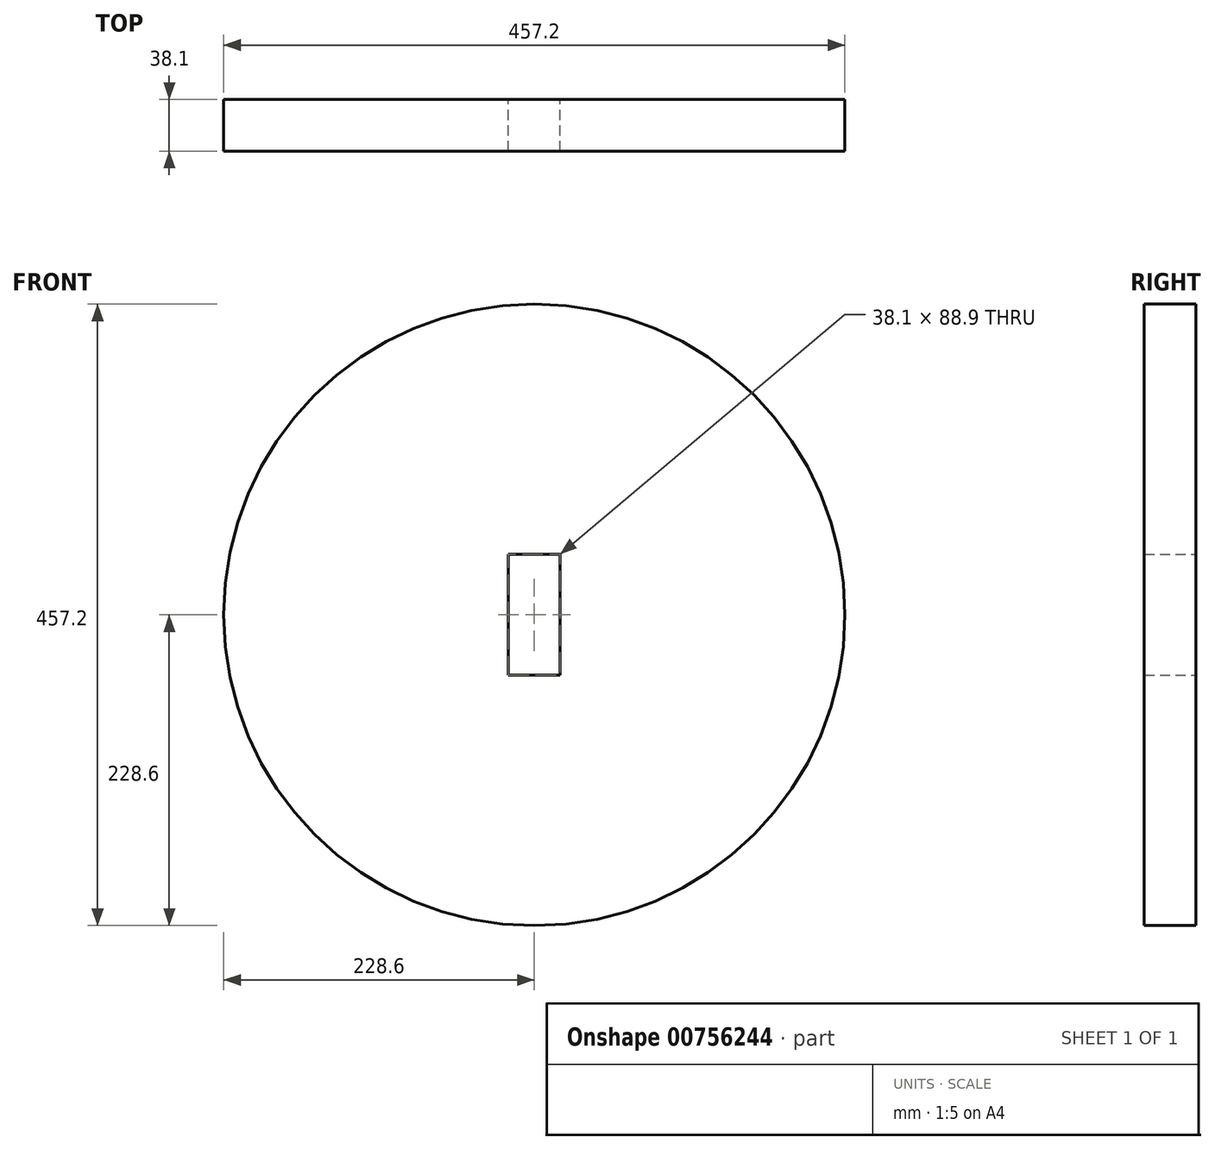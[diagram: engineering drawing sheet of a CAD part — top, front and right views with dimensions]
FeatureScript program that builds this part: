
annotation { "Feature Type Name" : "Feature", "Feature Type Description" : "" }
export const myFeature = defineFeature(function(context is Context, id is Id, definition is map)
    precondition{}
    {
        {
            var Q0;
            Q0=qCreatedBy(makeId("Front.planeOp"),FACE);
            var sketch = newSketch(context, id + "F0", { "sketchPlane" : qUnion([Q0])});
            skCircle(sketch, "E0", {"center": v(0, 0) * mm, "radius": 228.6 * mm});
            skLineSegment(sketch, "E1.bottom", {"start": v(-19.05, 44.45) * mm, "end": v(19.05, 44.45) * mm});
            skLineSegment(sketch, "E1.top", {"start": v(-19.05, -44.45) * mm, "end": v(19.05, -44.45) * mm});
            skLineSegment(sketch, "E1.left", {"start": v(-19.05, 44.45) * mm, "end": v(-19.05, -44.45) * mm});
            skLineSegment(sketch, "E1.right", {"start": v(19.05, 44.45) * mm, "end": v(19.05, -44.45) * mm});
            skSolve(sketch);
        }
        {
            var Q0;
            Q0=makeQuery(id+"F0.imprint","IMPRINT",FACE,{"disambiguationData":[TD([[makeQuery(id+"F0.imprint","IMPRINT",EDGE,{"derivedFrom":sQuery(id+"F0.wireOp",EDGE,"E0")}),1.0]])]});
            extrude(context, id + "F1", {"entities" : qUnion([Q0]), "endBound" : BoundingType.SYMMETRIC, "depth" : 38.1 * mm, "offsetDistance" : 25.4 * mm});
        }
    });
